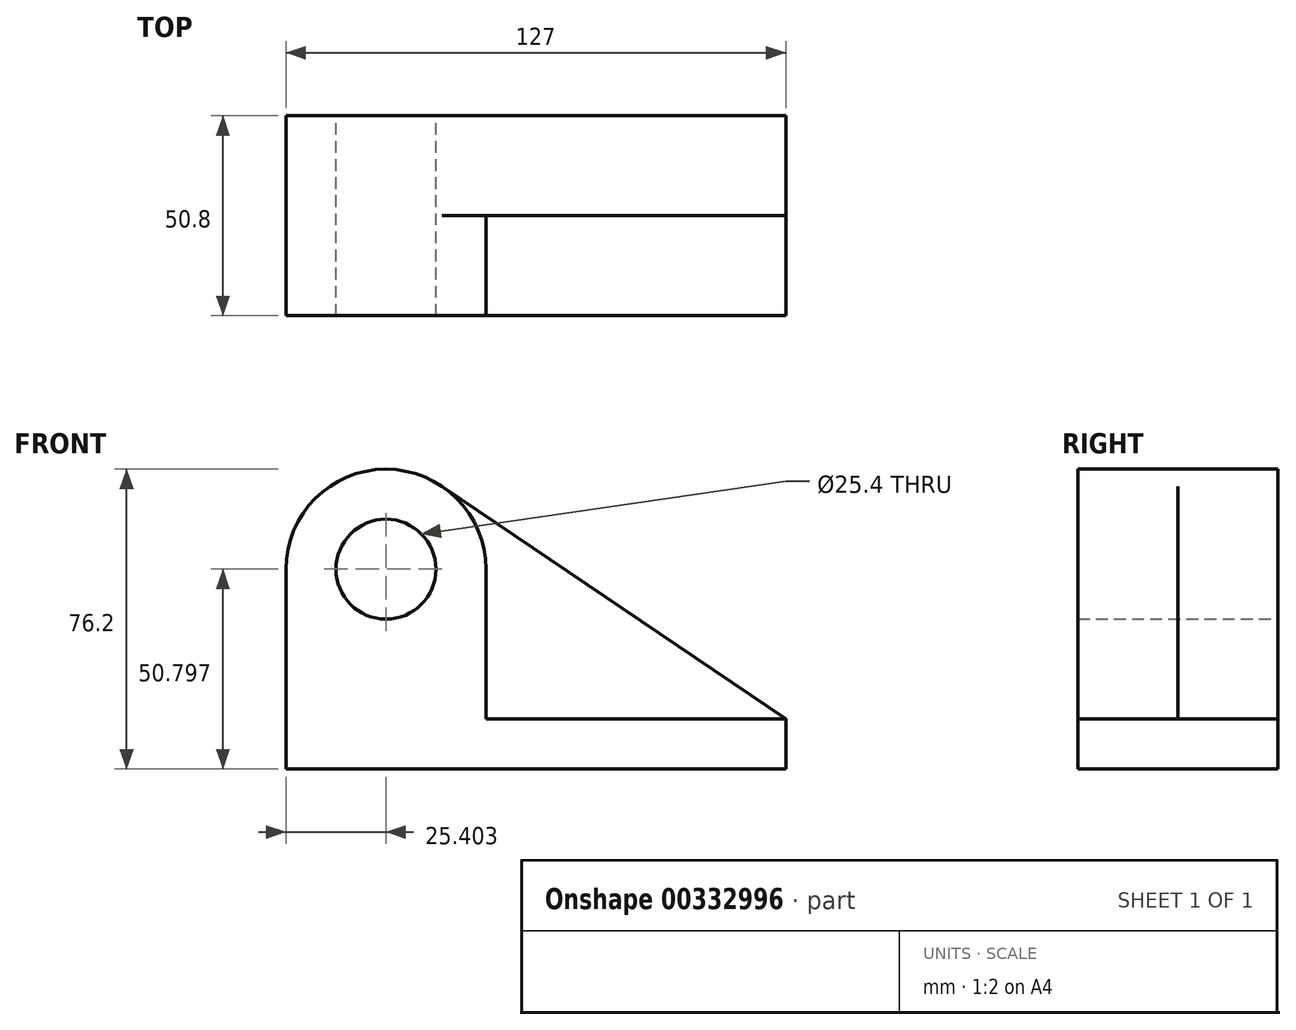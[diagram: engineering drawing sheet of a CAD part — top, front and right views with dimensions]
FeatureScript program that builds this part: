
annotation { "Feature Type Name" : "Feature", "Feature Type Description" : "" }
export const myFeature = defineFeature(function(context is Context, id is Id, definition is map)
    precondition{}
    {
        {
            var Q0;
            Q0=qCreatedBy(makeId("Front.planeOp"),FACE);
            var sketch = newSketch(context, id + "F0", { "sketchPlane" : qUnion([Q0])});
            skCircle(sketch, "E0", {"center": v(-56.39, 54.57) * mm, "radius": 12.7 * mm});
            skArc(sketch, "E1", {"start": v(-42.15, 75.6) * mm, "mid": v(-68.3, 77) * mm, "end": v(-81.79, 54.57) * mm});
            skLineSegment(sketch, "E2", {"start": v(-81.79, 54.57) * mm, "end": v(-81.79, 3.77) * mm});
            skLineSegment(sketch, "E3", {"start": v(45.21, 3.77) * mm, "end": v(-81.79, 3.77) * mm});
            skLineSegment(sketch, "E4", {"start": v(45.21, 16.47) * mm, "end": v(45.21, 3.77) * mm});
            skLineSegment(sketch, "E5", {"start": v(45.21, 16.47) * mm, "end": v(-42.15, 75.6) * mm});
            skSolve(sketch);
        }
        {
            var Q0;
            Q0=makeQuery(id+"F0.imprint","IMPRINT",FACE,{"disambiguationData":[TD([[makeQuery(id+"F0.imprint","IMPRINT",EDGE,{"derivedFrom":sQuery(id+"F0.wireOp",EDGE,"E0")}),-1.0]])]});
            extrude(context, id + "F1", {"entities" : qUnion([Q0]), "depth" : 25.4 * mm});
        }
        {
            var Q0;
            Q0=makeQuery(id+"F1.opExtrude","CAP_FACE",FACE,{"disambiguationData":[OSD([sQuery(id+"F0.wireOp",EDGE,"E0"),sQuery(id+"F0.wireOp",EDGE,"E1"),sQuery(id+"F0.wireOp",EDGE,"E2"),sQuery(id+"F0.wireOp",EDGE,"E3"),sQuery(id+"F0.wireOp",EDGE,"E4"),sQuery(id+"F0.wireOp",EDGE,"E5")])],"isStart":false});
            var sketch = newSketch(context, id + "F2", { "sketchPlane" : qUnion([Q0])});
            skCircle(sketch, "E6", {"center": v(-56.39, 54.57) * mm, "radius": 12.7 * mm});
            skArc(sketch, "E7", {"start": v(-30.99, 54.57) * mm, "mid": v(-56.39, 79.97) * mm, "end": v(-81.79, 54.57) * mm});
            skLineSegment(sketch, "E8.bottom", {"start": v(45.21, 16.47) * mm, "end": v(-30.99, 16.47) * mm});
            skLineSegment(sketch, "E8.top", {"start": v(45.21, 3.77) * mm, "end": v(-81.79, 3.77) * mm});
            skLineSegment(sketch, "E8.left", {"start": v(45.21, 16.47) * mm, "end": v(45.21, 3.77) * mm});
            skLineSegment(sketch, "E8.right", {"start": v(-81.79, 16.47) * mm, "end": v(-81.79, 3.77) * mm});
            skLineSegment(sketch, "E9", {"start": v(-30.99, 54.57) * mm, "end": v(-30.99, 16.47) * mm});
            skSolve(sketch);
        }
        {
            var Q0;
            Q0=makeQuery(id+"F2.imprint","IMPRINT",FACE,{"disambiguationData":[TD([[makeQuery(id+"F2.imprint","IMPRINT",EDGE,{"derivedFrom":sQuery(id+"F2.wireOp",EDGE,"E8.bottom")}),1.0]])]});
            extrude(context, id + "F3", {"entities" : qUnion([Q0]), "operationType" : NewBodyOperationType.ADD, "depth" : 25.4 * mm});
        }
    });
